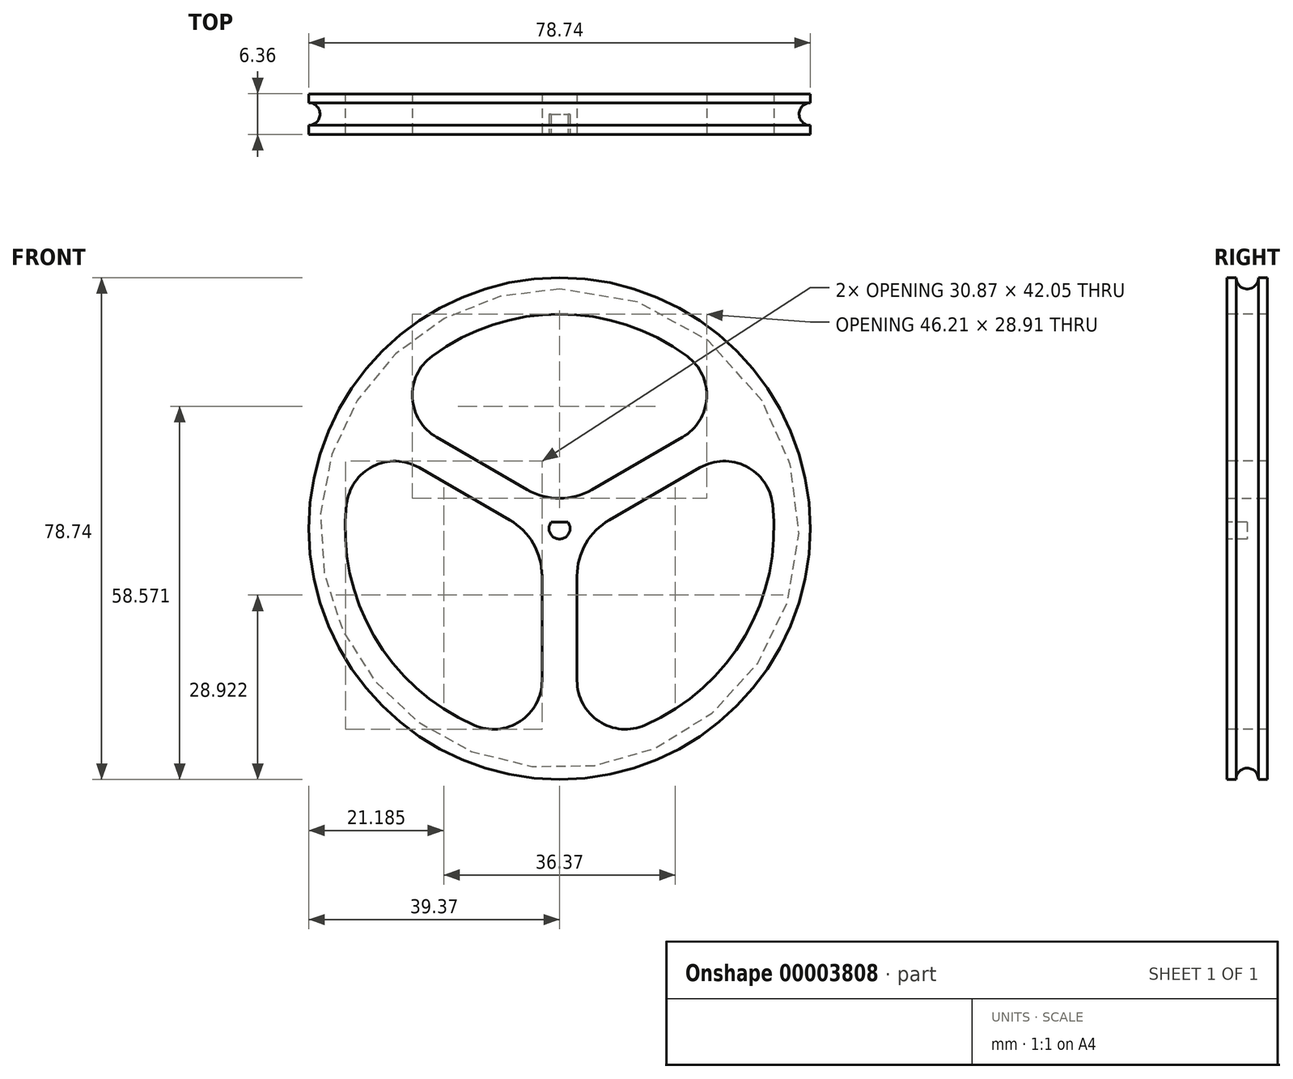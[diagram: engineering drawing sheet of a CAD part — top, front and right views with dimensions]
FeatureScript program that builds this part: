
annotation { "Feature Type Name" : "Feature", "Feature Type Description" : "" }
export const myFeature = defineFeature(function(context is Context, id is Id, definition is map)
    precondition{}
    {
        {
            var Q0;
            Q0=qCreatedBy(makeId("Front.planeOp"),FACE);
            var sketch = newSketch(context, id + "F0", { "sketchPlane" : qUnion([Q0])});
            skCircle(sketch, "E0", {"center": v(0, 0) * mm, "radius": 39.37 * mm});
            skSolve(sketch);
        }
        {
            var Q0;
            Q0=qSketchRegion(id+"F0",true);
            extrude(context, id + "F1", {"entities" : qUnion([Q0]), "oppositeDirection" : true, "depth" : 3.17 * mm});
        }
        {
            var Q0;
            Q0=qSketchRegion(id+"F0",true);
            extrude(context, id + "F2", {"entities" : qUnion([Q0]), "operationType" : NewBodyOperationType.ADD, "depth" : 3.17 * mm});
        }
        {
            var Q0;
            Q0=qCreatedBy(makeId("Right.planeOp"),FACE);
            var sketch = newSketch(context, id + "F3", { "sketchPlane" : qUnion([Q0])});
            skCircle(sketch, "E1", {"center": v(0, 39.37) * mm, "radius": 1.77 * mm});
            skLineSegment(sketch, "E2", {"start": v(0, 0) * mm, "end": v(24.73, 0) * mm, "construction": true});
            skSolve(sketch);
        }
        {
            var Q0;
            Q0=qSketchRegion(id+"F3",true);
            var Q1;
            Q1=sQuery(id+"F3.wireOp",EDGE,"E2");
            revolve(context, id + "F4", {"operationType" : NewBodyOperationType.REMOVE, "entities" : qUnion([Q0]), "axis" : qUnion([Q1]), "revolveType" : RevolveType.FULL, "oppositeDirection" : true});
        }
        {
            var Q0;
            Q0=makeQuery(id+"F2.opExtrude","CAP_FACE",FACE,{"disambiguationData":[OSD([sQuery(id+"F0.wireOp",EDGE,"E0")])],"isStart":false});
            var sketch = newSketch(context, id + "F5", { "sketchPlane" : qUnion([Q0])});
            skArc(sketch, "E3", {"start": v(-1.31, 1) * mm, "mid": v(0, -1.65) * mm, "end": v(1.31, 1) * mm});
            skLineSegment(sketch, "E4", {"start": v(-1.31, 1) * mm, "end": v(1.31, 1) * mm});
            skSolve(sketch);
        }
        {
            var Q0;
            Q0=qSketchRegion(id+"F5",true);
            extrude(context, id + "F6", {"entities" : qUnion([Q0]), "operationType" : NewBodyOperationType.REMOVE, "oppositeDirection" : true, "depth" : 3.17 * mm});
        }
        {
            var Q0;
            Q0=makeQuery(id+"F2.opExtrude","CAP_FACE",FACE,{"disambiguationData":[OSD([sQuery(id+"F0.wireOp",EDGE,"E0")])],"isStart":false});
            var sketch = newSketch(context, id + "F7", { "sketchPlane" : qUnion([Q0])});
            skCircle(sketch, "E5", {"center": v(0, 0) * mm, "radius": 33.66 * mm, "construction": true});
            skLineSegment(sketch, "E6", {"start": v(0, 0) * mm, "end": v(29.15, 16.83) * mm, "construction": true});
            skLineSegment(sketch, "E7", {"start": v(0, 0) * mm, "end": v(-29.15, 16.83) * mm, "construction": true});
            skLineSegment(sketch, "E8", {"start": v(0, 0) * mm, "end": v(0, 33.66) * mm, "construction": true});
            skLineSegment(sketch, "E9", {"start": v(0, 3.17) * mm, "end": v(-27.67, 19.15) * mm, "construction": true});
            skLineSegment(sketch, "E10", {"start": v(0, 3.17) * mm, "end": v(27.67, 19.15) * mm, "construction": true});
            skArc(sketch, "E11", {"start": v(27.67, 19.15) * mm, "mid": v(0, 33.66) * mm, "end": v(-27.67, 19.15) * mm, "construction": true});
            skLineSegment(sketch, "E12", {"start": v(-27.67, 19.15) * mm, "end": v(0, 3.18) * mm});
            skLineSegment(sketch, "E13", {"start": v(0, 3.17) * mm, "end": v(27.67, 19.15) * mm});
            skArc(sketch, "E14", {"start": v(27.67, 19.15) * mm, "mid": v(0, 33.66) * mm, "end": v(-27.67, 19.15) * mm});
            skArc(sketch, "E15.1.0", {"start": v(-30.42, 14.39) * mm, "mid": v(-29.15, -16.83) * mm, "end": v(-2.75, -33.54) * mm});
            skLineSegment(sketch, "E15.1.1", {"start": v(-2.75, -33.54) * mm, "end": v(-2.75, -1.59) * mm});
            skLineSegment(sketch, "E15.1.2", {"start": v(-2.75, -1.59) * mm, "end": v(-30.42, 14.39) * mm});
            skLineSegment(sketch, "E15.anchor1", {"start": v(0, 0) * mm, "end": v(-27.67, 19.15) * mm, "construction": true});
            skLineSegment(sketch, "E15.anchor2", {"start": v(0, 0) * mm, "end": v(30.42, 14.39) * mm, "construction": true});
            skArc(sketch, "E16.3.2.0", {"start": v(2.75, -33.54) * mm, "mid": v(29.15, -16.83) * mm, "end": v(30.42, 14.39) * mm});
            skLineSegment(sketch, "E16.4.2.0", {"start": v(30.42, 14.39) * mm, "end": v(2.75, -1.59) * mm});
            skLineSegment(sketch, "E16.7.2.0", {"start": v(2.75, -1.59) * mm, "end": v(2.75, -33.54) * mm});
            skSolve(sketch);
        }
        {
            var Q0;
            Q0=makeQuery(id+"F7.imprint","IMPRINT",FACE,{"disambiguationData":[TD([[makeQuery(id+"F7.imprint","IMPRINT",EDGE,{"derivedFrom":sQuery(id+"F7.wireOp",EDGE,"E12")}),1.0]])]});
            var Q1;
            Q1=makeQuery(id+"F7.imprint","IMPRINT",FACE,{"disambiguationData":[TD([[makeQuery(id+"F7.imprint","IMPRINT",EDGE,{"derivedFrom":sQuery(id+"F7.wireOp",EDGE,"E16.3.2.0")}),1.0]])]});
            var Q2;
            Q2=makeQuery(id+"F7.imprint","IMPRINT",FACE,{"disambiguationData":[TD([[makeQuery(id+"F7.imprint","IMPRINT",EDGE,{"derivedFrom":sQuery(id+"F7.wireOp",EDGE,"E15.1.0")}),1.0]])]});
            extrude(context, id + "F8", {"entities" : qUnion([Q0, Q1, Q2]), "operationType" : NewBodyOperationType.REMOVE, "endBound" : BoundingType.THROUGH_ALL, "oppositeDirection" : true, "depth" : 25.4 * mm});
        }
        {
            var Q0;
            Q0=makeQuery(id+"F8.boolean.opBoolean","COPY",EDGE,{"derivedFrom":makeQuery(id+"F8.opExtrude","SWEPT_EDGE",EDGE,{"disambiguationData":[OSD([sQuery(id+"F7.wireOp",EDGE,"E13"),sQuery(id+"F7.wireOp",EDGE,"E14")])]})});
            var Q1;
            Q1=makeQuery(id+"F8.boolean.opBoolean","COPY",EDGE,{"derivedFrom":makeQuery(id+"F8.opExtrude","SWEPT_EDGE",EDGE,{"disambiguationData":[OSD([sQuery(id+"F7.wireOp",EDGE,"E12"),sQuery(id+"F7.wireOp",EDGE,"E14")])]})});
            var Q2;
            Q2=makeQuery(id+"F8.boolean.opBoolean","COPY",EDGE,{"derivedFrom":makeQuery(id+"F8.opExtrude","SWEPT_EDGE",EDGE,{"disambiguationData":[OSD([sQuery(id+"F7.wireOp",EDGE,"E15.1.0"),sQuery(id+"F7.wireOp",EDGE,"E15.1.1")])]})});
            var Q3;
            Q3=makeQuery(id+"F8.boolean.opBoolean","COPY",EDGE,{"derivedFrom":makeQuery(id+"F8.opExtrude","SWEPT_EDGE",EDGE,{"disambiguationData":[OSD([sQuery(id+"F7.wireOp",EDGE,"E16.3.2.0"),sQuery(id+"F7.wireOp",EDGE,"E16.7.2.0")])]})});
            var Q4;
            Q4=makeQuery(id+"F8.boolean.opBoolean","COPY",EDGE,{"derivedFrom":makeQuery(id+"F8.opExtrude","SWEPT_EDGE",EDGE,{"disambiguationData":[OSD([sQuery(id+"F7.wireOp",EDGE,"E15.1.0"),sQuery(id+"F7.wireOp",EDGE,"E15.1.2")])]})});
            var Q5;
            Q5=makeQuery(id+"F8.boolean.opBoolean","COPY",EDGE,{"derivedFrom":makeQuery(id+"F8.opExtrude","SWEPT_EDGE",EDGE,{"disambiguationData":[OSD([sQuery(id+"F7.wireOp",EDGE,"E16.3.2.0"),sQuery(id+"F7.wireOp",EDGE,"E16.4.2.0")])]})});
            fillet(context, id + "F9", {"entities" : qUnion([Q0, Q1, Q2, Q3, Q4, Q5]), "radius" : 7.62 * mm, "tangentPropagation" : true, "allowEdgeOverflow" : false});
        }
        {
            var Q0;
            Q0=makeQuery(id+"F8.boolean.opBoolean","COPY",EDGE,{"derivedFrom":makeQuery(id+"F8.opExtrude","SWEPT_EDGE",EDGE,{"disambiguationData":[OSD([sQuery(id+"F7.wireOp",EDGE,"E12"),sQuery(id+"F7.wireOp",EDGE,"E13")])]})});
            var Q1;
            Q1=makeQuery(id+"F8.boolean.opBoolean","COPY",EDGE,{"derivedFrom":makeQuery(id+"F8.opExtrude","SWEPT_EDGE",EDGE,{"disambiguationData":[OSD([sQuery(id+"F7.wireOp",EDGE,"E15.1.1"),sQuery(id+"F7.wireOp",EDGE,"E15.1.2")])]})});
            var Q2;
            Q2=makeQuery(id+"F8.boolean.opBoolean","COPY",EDGE,{"derivedFrom":makeQuery(id+"F8.opExtrude","SWEPT_EDGE",EDGE,{"disambiguationData":[OSD([sQuery(id+"F7.wireOp",EDGE,"E16.4.2.0"),sQuery(id+"F7.wireOp",EDGE,"E16.7.2.0")])]})});
            fillet(context, id + "F10", {"entities" : qUnion([Q0, Q1, Q2]), "radius" : 10.16 * mm, "tangentPropagation" : true, "allowEdgeOverflow" : false});
        }
    });
